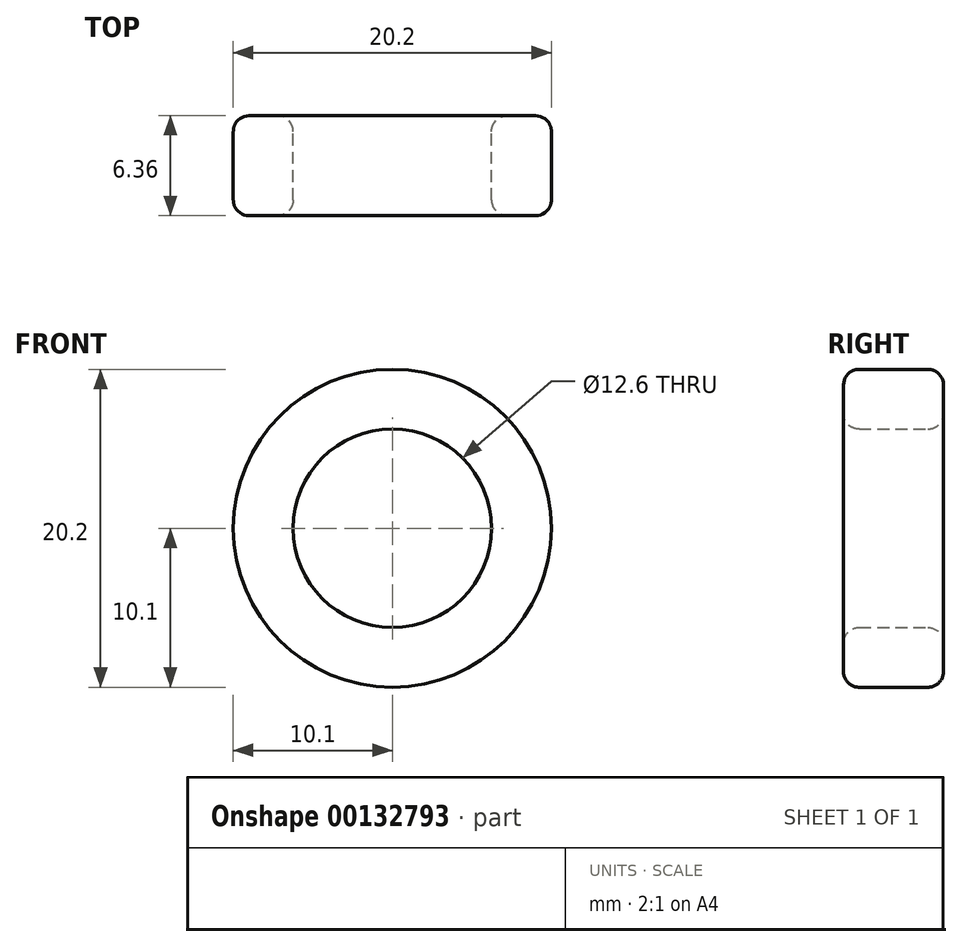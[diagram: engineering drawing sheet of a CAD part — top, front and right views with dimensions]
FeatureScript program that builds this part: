
annotation { "Feature Type Name" : "Feature", "Feature Type Description" : "" }
export const myFeature = defineFeature(function(context is Context, id is Id, definition is map)
    precondition{}
    {
        {
            var Q0;
            Q0=qCreatedBy(makeId("Front.planeOp"),FACE);
            var sketch = newSketch(context, id + "F0", { "sketchPlane" : qUnion([Q0])});
            skCircle(sketch, "E0", {"center": v(0, 0) * mm, "radius": 10.1 * mm});
            skCircle(sketch, "E1", {"center": v(0, 0) * mm, "radius": 6.3 * mm});
            skSolve(sketch);
        }
        {
            var Q0;
            Q0=makeQuery(id+"F0.imprint","IMPRINT",FACE,{"disambiguationData":[TD([[makeQuery(id+"F0.imprint","IMPRINT",EDGE,{"derivedFrom":sQuery(id+"F0.wireOp",EDGE,"E0")}),1.0]])]});
            extrude(context, id + "F1", {"entities" : qUnion([Q0]), "endBound" : BoundingType.SYMMETRIC, "depth" : 6.35 * mm});
        }
        {
            var Q0;
            Q0=makeQuery(id+"F1.opExtrude","CAP_EDGE",EDGE,{"disambiguationData":[OSD([sQuery(id+"F0.wireOp",EDGE,"E1")])],"isStart":false});
            var Q1;
            Q1=makeQuery(id+"F1.opExtrude","CAP_EDGE",EDGE,{"disambiguationData":[OSD([sQuery(id+"F0.wireOp",EDGE,"E0")])],"isStart":false});
            var Q2;
            Q2=makeQuery(id+"F1.opExtrude","CAP_EDGE",EDGE,{"disambiguationData":[OSD([sQuery(id+"F0.wireOp",EDGE,"E1")])],"isStart":true});
            var Q3;
            Q3=makeQuery(id+"F1.opExtrude","CAP_EDGE",EDGE,{"disambiguationData":[OSD([sQuery(id+"F0.wireOp",EDGE,"E0")])],"isStart":true});
            fillet(context, id + "F2", {"entities" : qUnion([Q0, Q1, Q2, Q3]), "radius" : 1 * mm, "tangentPropagation" : true, "allowEdgeOverflow" : false});
        }
    });
